# Revit family: Locker_Benches_ADA-Salsbury_Industries-Aluminum_77770_Series
name_source: partatom
category: Specialty Equipment
revit_build: Autodesk Revit 2016 (Build: 20190507_1515(x64)
units: mm (PartAtom-declared; Revit-internal decimal feet)

## family parameters
Always vertical = Yes
Cut with Voids When Loaded = No
OmniClass Number = 23.40.00.00
OmniClass Title = Equipment and Furnishings
Part Type = Normal
Room Calculation Point = No
Round Connector Dimension = Use Diameter
Shared = No
Work Plane-Based = No

## types (4) — shared parameters
ADA Guidelines = https://www.lockers.com
Assembly Code = C1030310
Description = Americans with Disabilities Act (ADA) compliant
Manufacturer = Salsbury Industries
MasterFormat Number = 10 51 53
MasterFormat Title = Locker Room Benches
OmniClass 23 Number = 23.40.00.00
OmniClass 23 Title = Equipment and Furnishings
Primary Material = Aluminum - Salsbury Finish - Aluminum
Seat Height = 18 "
Secondary Material = Paint - Salsbury Finish - Aluminum
URL = www.lockers.com
Version = 1.0 (11/16/18)

## per-type parameters (varying)
| type | Back Support | Depth | Height | Pedestal Height Offset | Pedestal Top Plate | Plank Length | Type Comments | Vertical Plank Length | Width |
| 77771-ADA | No | 20 " | 18 " | 16 " | Yes | Aluminum Bench Plank_77770_Series : 42" Wide Plank | Aluminum ADA Locker Bench | Aluminum Bench Plank_77770_Series - Vertical : 42" Wide Plank | 42 " |
| 77771-ADAB | Yes | 23 " | 39 " | 15 " | No | Aluminum Bench Plank_77770_Series : 42" Wide Plank | Aluminum ADA Locker Bench with Back Support | Aluminum Bench Plank_77770_Series - Vertical : 42" Wide Plank | 42 " |
| 77772-ADAB | Yes | 23 " | 39 " | 15 " | No | Aluminum Bench Plank_77770_Series : 48" Wide Plank | Aluminum ADA Locker Bench with Back Support | Aluminum Bench Plank_77770_Series - Vertical : 48" Wide Plank | 48 " |
| 77772-ADA | No | 20 " | 18 " | 16 " | Yes | Aluminum Bench Plank_77770_Series : 48" Wide Plank | Aluminum ADA Locker Bench | Aluminum Bench Plank_77770_Series - Vertical : 48" Wide Plank | 48 " |

note: column(s) folded — value = type name in every type: Model

## geometry (parser evidence)
native form markers: Sweep x7
no freeform markers — native parametric forms only
